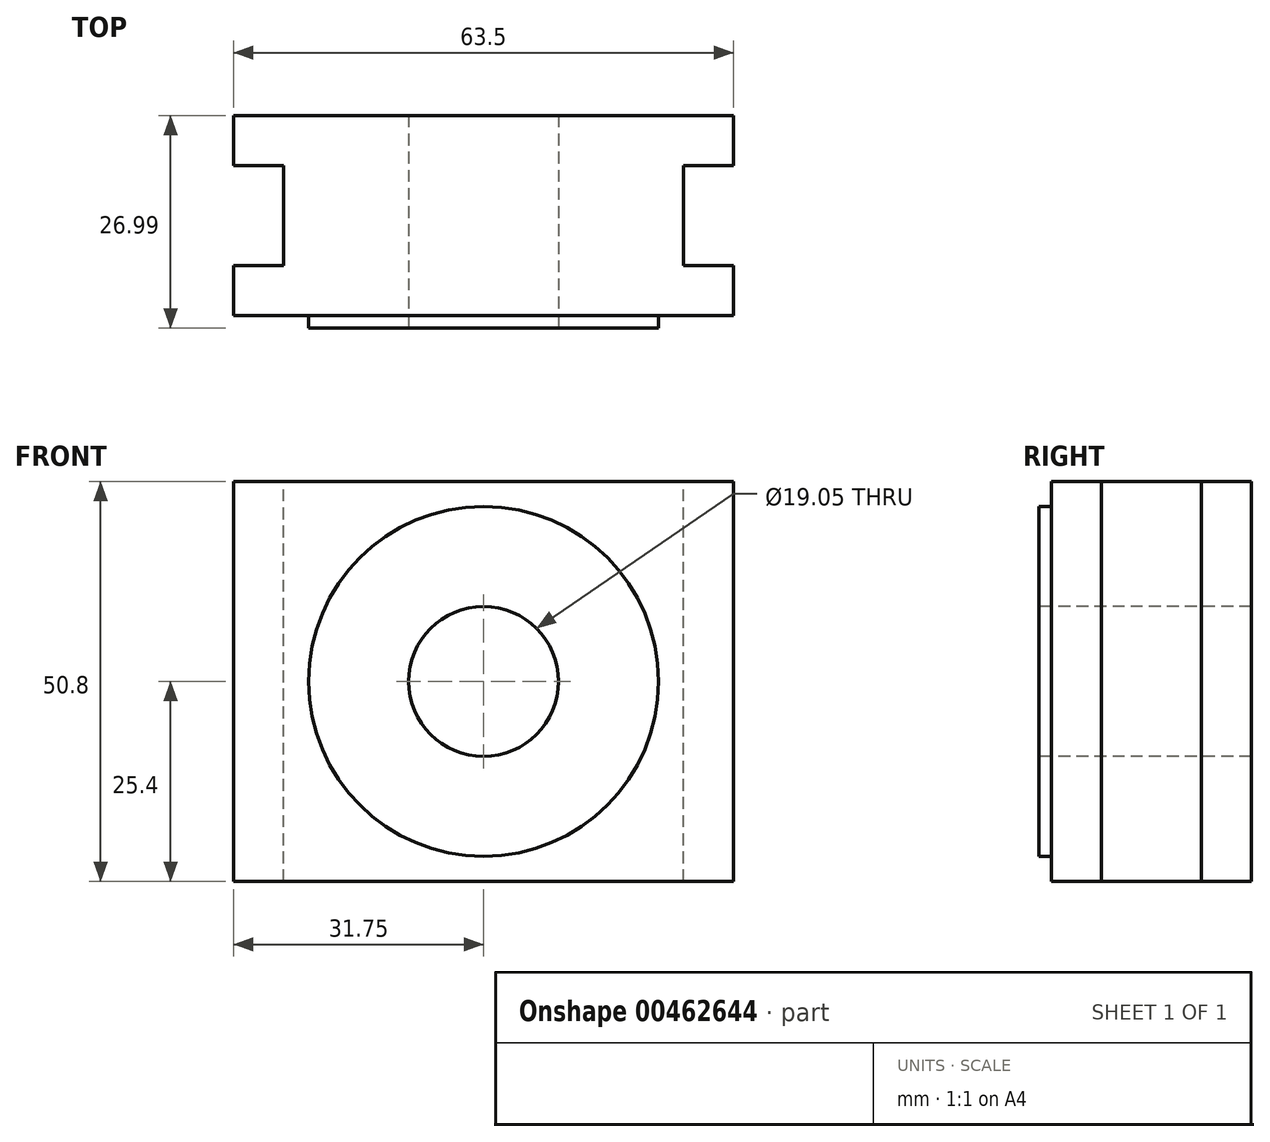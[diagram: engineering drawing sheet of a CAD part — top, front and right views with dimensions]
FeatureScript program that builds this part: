
annotation { "Feature Type Name" : "Feature", "Feature Type Description" : "" }
export const myFeature = defineFeature(function(context is Context, id is Id, definition is map)
    precondition{}
    {
        {
            var Q0;
            Q0=qCreatedBy(makeId("Front.planeOp"),FACE);
            var sketch = newSketch(context, id + "F0", { "sketchPlane" : qUnion([Q0])});
            skLineSegment(sketch, "E0.bottom", {"start": v(25.4, -25.4) * mm, "end": v(-25.4, -25.4) * mm});
            skLineSegment(sketch, "E0.top", {"start": v(25.4, 25.4) * mm, "end": v(-25.4, 25.4) * mm});
            skLineSegment(sketch, "E0.left", {"start": v(25.4, -25.4) * mm, "end": v(25.4, 25.4) * mm});
            skLineSegment(sketch, "E0.right", {"start": v(-25.4, -25.4) * mm, "end": v(-25.4, 25.4) * mm});
            skPoint(sketch, "E0.middle", {"position": v(0, 0) * mm});
            skSolve(sketch);
        }
        {
            var Q0;
            Q0 = qSketchRegion(id + "F0", true);
            var Q1;
            Q1 = qSketchRegion(id + "F2", true);
            extrude(context, id + "F1", {"entities" : qUnion([Q0, Q1]), "depth" : 12.7 * mm});
        }
        {
            var Q0;
            Q0=makeQuery(id+"F1.opExtrude","CAP_FACE",FACE,{"disambiguationData":[OSD([sQuery(id+"F0.wireOp",EDGE,"E0.bottom"),sQuery(id+"F0.wireOp",EDGE,"E0.top"),sQuery(id+"F0.wireOp",EDGE,"E0.left"),sQuery(id+"F0.wireOp",EDGE,"E0.right")])],"isStart":false});
            var sketch = newSketch(context, id + "F2", { "sketchPlane" : qUnion([Q0])});
            skLineSegment(sketch, "E1.bottom", {"start": v(31.75, -25.4) * mm, "end": v(-31.75, -25.4) * mm});
            skLineSegment(sketch, "E1.top", {"start": v(31.75, 25.4) * mm, "end": v(-31.75, 25.4) * mm});
            skLineSegment(sketch, "E1.left", {"start": v(31.75, -25.4) * mm, "end": v(31.75, 25.4) * mm});
            skLineSegment(sketch, "E1.right", {"start": v(-31.75, -25.4) * mm, "end": v(-31.75, 25.4) * mm});
            skPoint(sketch, "E1.middle", {"position": v(0, 0) * mm});
            skSolve(sketch);
        }
        {
            var Q0;
            {var subQ2=sQuery(id+"F2.wireOp",EDGE,"E1.right");Q0=makeQuery(id+"F2.imprint","IMPRINT",FACE,{"disambiguationData":[TD([[makeQuery(id+"F2.imprint","IMPRINT",EDGE,{"derivedFrom":subQ2}),-1.0]])]});}
            var Q1;
            {var subQ1=makeQuery(id+"F1.opExtrude","CAP_EDGE",EDGE,{"disambiguationData":[OSD([sQuery(id+"F0.wireOp",EDGE,"E0.left")])],"isStart":false});Q1=makeQuery(id+"F2.imprint","IMPRINT",FACE,{"disambiguationData":[TD([[makeQuery(id+"F2.imprint","IMPRINT",EDGE,{"derivedFrom":subQ1}),1.0]])]});}
            var Q2;
            {var subQ2=sQuery(id+"F2.wireOp",EDGE,"E1.left");Q2=makeQuery(id+"F2.imprint","IMPRINT",FACE,{"disambiguationData":[TD([[makeQuery(id+"F2.imprint","IMPRINT",EDGE,{"derivedFrom":subQ2}),1.0]])]});}
            extrude(context, id + "F3", {"entities" : qUnion([Q0, Q1, Q2]), "operationType" : NewBodyOperationType.ADD, "depth" : 6.35 * mm});
        }
        {
            var Q0;
            Q0=makeQuery(id+"F1.opExtrude","CAP_FACE",FACE,{"disambiguationData":[OSD([sQuery(id+"F0.wireOp",EDGE,"E0.bottom"),sQuery(id+"F0.wireOp",EDGE,"E0.top"),sQuery(id+"F0.wireOp",EDGE,"E0.left"),sQuery(id+"F0.wireOp",EDGE,"E0.right")])],"isStart":true});
            var sketch = newSketch(context, id + "F4", { "sketchPlane" : qUnion([Q0])});
            skLineSegment(sketch, "E2.bottom", {"start": v(-31.75, -25.4) * mm, "end": v(31.75, -25.4) * mm});
            skLineSegment(sketch, "E2.top", {"start": v(-31.75, 25.4) * mm, "end": v(31.75, 25.4) * mm});
            skLineSegment(sketch, "E2.left", {"start": v(-31.75, -25.4) * mm, "end": v(-31.75, 25.4) * mm});
            skLineSegment(sketch, "E2.right", {"start": v(31.75, -25.4) * mm, "end": v(31.75, 25.4) * mm});
            skPoint(sketch, "E2.middle", {"position": v(0, 0) * mm});
            skSolve(sketch);
        }
        {
            var Q0;
            {var subQ2=sQuery(id+"F4.wireOp",EDGE,"E2.right");Q0=makeQuery(id+"F4.imprint","IMPRINT",FACE,{"disambiguationData":[TD([[makeQuery(id+"F4.imprint","IMPRINT",EDGE,{"derivedFrom":subQ2}),1.0]])]});}
            var Q1;
            {var subQ1=makeQuery(id+"F1.opExtrude","CAP_EDGE",EDGE,{"disambiguationData":[OSD([sQuery(id+"F0.wireOp",EDGE,"E0.left")])],"isStart":true});Q1=makeQuery(id+"F4.imprint","IMPRINT",FACE,{"disambiguationData":[TD([[makeQuery(id+"F4.imprint","IMPRINT",EDGE,{"derivedFrom":subQ1}),-1.0]])]});}
            var Q2;
            {var subQ2=sQuery(id+"F4.wireOp",EDGE,"E2.left");Q2=makeQuery(id+"F4.imprint","IMPRINT",FACE,{"disambiguationData":[TD([[makeQuery(id+"F4.imprint","IMPRINT",EDGE,{"derivedFrom":subQ2}),-1.0]])]});}
            extrude(context, id + "F5", {"entities" : qUnion([Q0, Q1, Q2]), "operationType" : NewBodyOperationType.ADD, "depth" : 6.35 * mm});
        }
        {
            var Q0;
            Q0=makeQuery(id+"F3.opExtrude","CAP_FACE",FACE,{"disambiguationData":[OSD([sQuery(id+"F2.wireOp",EDGE,"E1.bottom"),sQuery(id+"F2.wireOp",EDGE,"E1.top"),sQuery(id+"F2.wireOp",EDGE,"E1.left"),sQuery(id+"F2.wireOp",EDGE,"E1.right")])],"isStart":false});
            var sketch = newSketch(context, id + "F6", { "sketchPlane" : qUnion([Q0])});
            skCircle(sketch, "E3", {"center": v(0, 0) * mm, "radius": 9.53 * mm});
            skSolve(sketch);
        }
        {
            var Q0;
            Q0 = qSketchRegion(id + "F6", true);
            extrude(context, id + "F7", {"entities" : qUnion([Q0]), "operationType" : NewBodyOperationType.REMOVE, "oppositeDirection" : true, "depth" : 38.1 * mm});
        }
        {
            var Q0;
            Q0=makeQuery(id+"F3.opExtrude","CAP_FACE",FACE,{"disambiguationData":[OSD([sQuery(id+"F2.wireOp",EDGE,"E1.bottom"),sQuery(id+"F2.wireOp",EDGE,"E1.top"),sQuery(id+"F2.wireOp",EDGE,"E1.left"),sQuery(id+"F2.wireOp",EDGE,"E1.right")])],"isStart":false});
            var sketch = newSketch(context, id + "F8", { "sketchPlane" : qUnion([Q0])});
            skCircle(sketch, "E4", {"center": v(0, 0) * mm, "radius": 22.23 * mm});
            skSolve(sketch);
        }
        {
            var Q0;
            Q0=makeQuery(id+"F8.imprint","IMPRINT",FACE,{"disambiguationData":[TD([[makeQuery(id+"F8.imprint","IMPRINT",EDGE,{"derivedFrom":sQuery(id+"F8.wireOp",EDGE,"E4")}),1.0]])]});
            var Q1;
            Q1=makeQuery(id+"F8.imprint","IMPRINT",FACE,{"disambiguationData":[TD([[makeQuery(id+"F8.imprint","IMPRINT",EDGE,{"derivedFrom":makeQuery(id+"F7.boolean.opBoolean","COPY",EDGE,{"derivedFrom":makeQuery(id+"F7.opExtrude","CAP_EDGE",EDGE,{"disambiguationData":[OSD([sQuery(id+"F6.wireOp",EDGE,"E3")])],"isStart":true})})}),1.0]])]});
            extrude(context, id + "F9", {"entities" : qUnion([Q0, Q1]), "operationType" : NewBodyOperationType.ADD, "depth" : 1.59 * mm});
        }
    });
